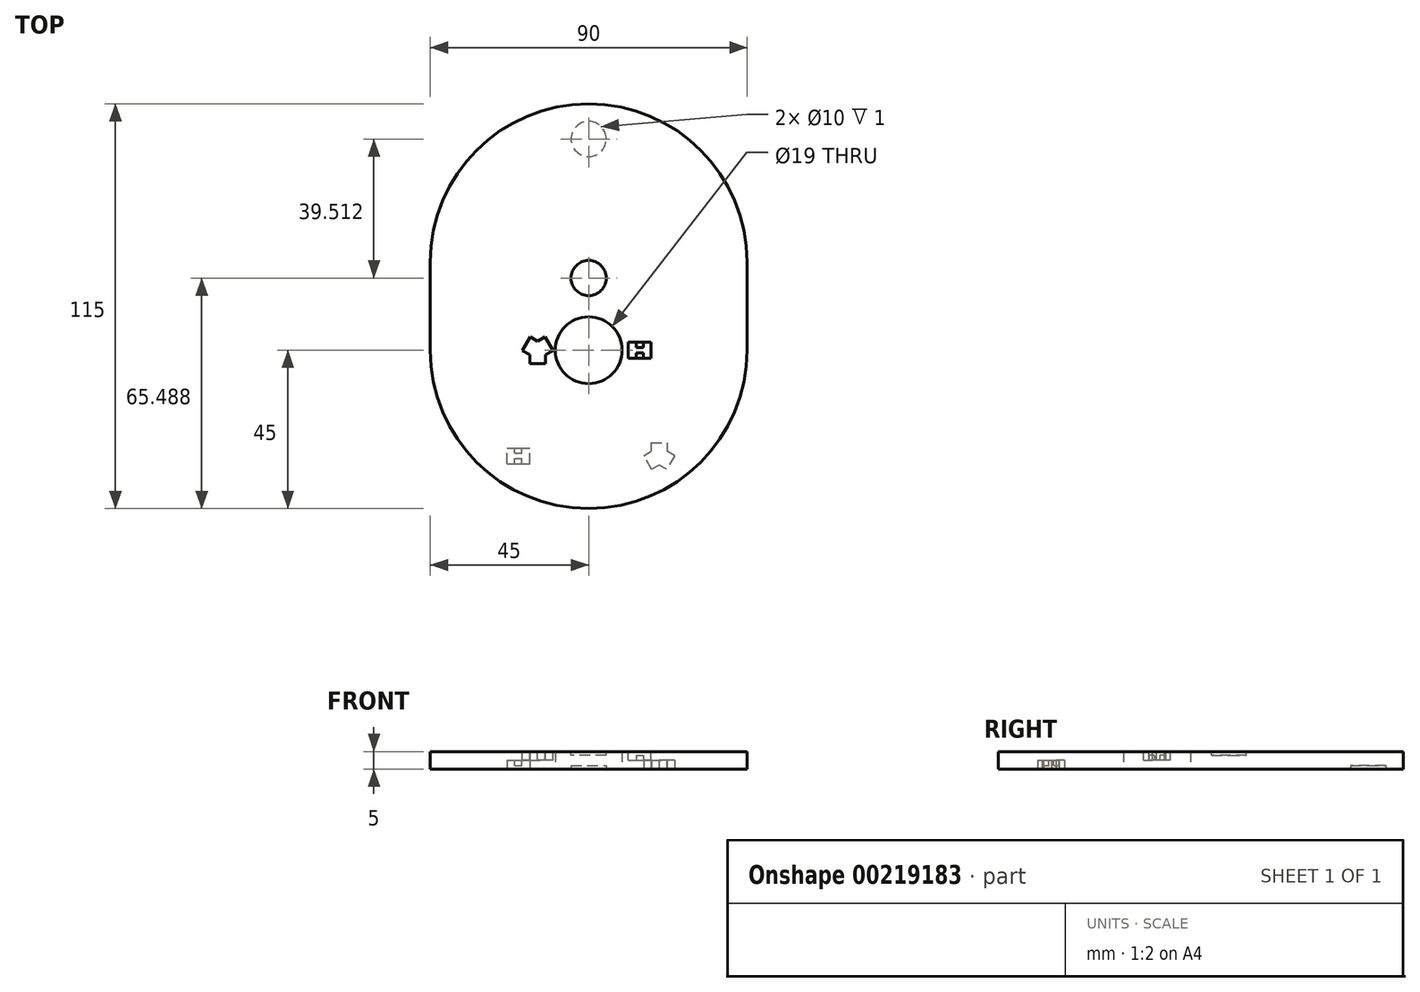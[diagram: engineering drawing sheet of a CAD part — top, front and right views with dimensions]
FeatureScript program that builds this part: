
annotation { "Feature Type Name" : "Feature", "Feature Type Description" : "" }
export const myFeature = defineFeature(function(context is Context, id is Id, definition is map)
    precondition{}
    {
        {
            var Q0;
            Q0=qCreatedBy(makeId("Top.planeOp"),FACE);
            var sketch = newSketch(context, id + "F0", { "sketchPlane" : qUnion([Q0])});
            skArc(sketch, "E0", {"start": v(-45, 0) * mm, "mid": v(0, -45) * mm, "end": v(45, 0) * mm});
            skLineSegment(sketch, "E1", {"start": v(-45, 0) * mm, "end": v(-45, 70) * mm});
            skLineSegment(sketch, "E2", {"start": v(-45, 70) * mm, "end": v(45, 70) * mm});
            skLineSegment(sketch, "E3", {"start": v(45, 70) * mm, "end": v(45, 0) * mm});
            skSolve(sketch);
        }
        {
            var Q0;
            Q0 = qSketchRegion(id + "F0", true);
            extrude(context, id + "F1", {"entities" : qUnion([Q0]), "depth" : 5 * mm});
        }
        {
            var Q0;
            Q0=makeQuery(id+"F1.opExtrude","CAP_FACE",FACE,{"disambiguationData":[OSD([sQuery(id+"F0.wireOp",EDGE,"E0")])],"isStart":false});
            var sketch = newSketch(context, id + "F2", { "sketchPlane" : qUnion([Q0])});
            skPoint(sketch, "E4", {"position": v(-14.5, 0) * mm});
            skLineSegment(sketch, "E5", {"start": v(-16.62, 3.83) * mm, "end": v(-18.87, -0.07) * mm});
            skLineSegment(sketch, "E6", {"start": v(-16.75, -3.75) * mm, "end": v(-12.25, -3.75) * mm});
            skLineSegment(sketch, "E7", {"start": v(-10.12, -0.07) * mm, "end": v(-12.37, 3.83) * mm});
            skLineSegment(sketch, "E8", {"start": v(-18.87, -0.07) * mm, "end": v(-16.75, -1.3) * mm});
            skLineSegment(sketch, "E9", {"start": v(-16.62, 3.83) * mm, "end": v(-14.5, 2.6) * mm});
            skLineSegment(sketch, "E10", {"start": v(-16.75, -3.75) * mm, "end": v(-16.75, -1.3) * mm});
            skLineSegment(sketch, "E11", {"start": v(-12.25, -3.75) * mm, "end": v(-12.25, -1.3) * mm});
            skLineSegment(sketch, "E12", {"start": v(-12.37, 3.83) * mm, "end": v(-14.5, 2.6) * mm});
            skLineSegment(sketch, "E13", {"start": v(-10.12, -0.07) * mm, "end": v(-12.25, -1.3) * mm});
            skPoint(sketch, "E14.orphan", {"position": v(-8, -3.75) * mm});
            skPoint(sketch, "E15.orphan", {"position": v(-14.5, 7.5) * mm});
            skPoint(sketch, "E16.orphan", {"position": v(-21, -3.75) * mm});
            skSolve(sketch);
        }
        {
            var Q0;
            Q0 = qSketchRegion(id + "F2", true);
            extrude(context, id + "F3", {"entities" : qUnion([Q0]), "operationType" : NewBodyOperationType.REMOVE, "oppositeDirection" : true, "depth" : 2.5 * mm});
        }
        {
            var Q0;
            Q0=makeQuery(id+"F1.opExtrude","CAP_FACE",FACE,{"disambiguationData":[OSD([sQuery(id+"F0.wireOp",EDGE,"E0")])],"isStart":false});
            var sketch = newSketch(context, id + "F4", { "sketchPlane" : qUnion([Q0])});
            skPoint(sketch, "E17", {"position": v(14.5, 0) * mm});
            skLineSegment(sketch, "E18.bottom", {"start": v(11.25, 2.25) * mm, "end": v(17.75, 2.25) * mm});
            skLineSegment(sketch, "E18.top", {"start": v(11.25, -2.25) * mm, "end": v(17.75, -2.25) * mm});
            skLineSegment(sketch, "E18.left", {"start": v(11.25, 2.25) * mm, "end": v(11.25, -2.25) * mm});
            skLineSegment(sketch, "E18.right", {"start": v(17.75, 2.25) * mm, "end": v(17.75, -2.25) * mm});
            skSolve(sketch);
        }
        {
            var Q0;
            Q0 = qSketchRegion(id + "F4", true);
            extrude(context, id + "F5", {"entities" : qUnion([Q0]), "operationType" : NewBodyOperationType.REMOVE, "oppositeDirection" : true, "depth" : 2.5 * mm});
        }
        {
            var Q0;
            Q0=makeQuery(id+"F5.boolean.opBoolean","COPY",FACE,{"derivedFrom":makeQuery(id+"F5.opExtrude","CAP_FACE",FACE,{"disambiguationData":[OSD([sQuery(id+"F4.wireOp",EDGE,"E18.bottom"),sQuery(id+"F4.wireOp",EDGE,"E18.top"),sQuery(id+"F4.wireOp",EDGE,"E18.left"),sQuery(id+"F4.wireOp",EDGE,"E18.right")])],"isStart":false})});
            var sketch = newSketch(context, id + "F6", { "sketchPlane" : qUnion([Q0])});
            skLineSegment(sketch, "E19.bottom", {"start": v(13.5, 2.25) * mm, "end": v(15.5, 2.25) * mm});
            skLineSegment(sketch, "E19.top", {"start": v(13.5, -2.25) * mm, "end": v(15.5, -2.25) * mm});
            skLineSegment(sketch, "E19.left", {"start": v(13.5, 2.25) * mm, "end": v(13.5, 0.75) * mm});
            skLineSegment(sketch, "E19.right", {"start": v(15.5, 2.25) * mm, "end": v(15.5, 0.75) * mm});
            skLineSegment(sketch, "E20", {"start": v(13.5, 0.75) * mm, "end": v(15.5, 0.75) * mm});
            skLineSegment(sketch, "E21", {"start": v(13.5, -0.75) * mm, "end": v(15.5, -0.75) * mm});
            skLineSegment(sketch, "E22.trimOffspring", {"start": v(13.5, -0.75) * mm, "end": v(13.5, -2.25) * mm});
            skLineSegment(sketch, "E23.trimOffspring", {"start": v(15.5, -0.75) * mm, "end": v(15.5, -2.25) * mm});
            skSolve(sketch);
        }
        {
            var Q0;
            Q0 = qSketchRegion(id + "F6", true);
            extrude(context, id + "F7", {"entities" : qUnion([Q0]), "operationType" : NewBodyOperationType.ADD, "depth" : 1.5 * mm});
        }
        {
            var Q0;
            Q0=makeQuery(id+"F1.opExtrude","CAP_FACE",FACE,{"disambiguationData":[OSD([sQuery(id+"F0.wireOp",EDGE,"E0")])],"isStart":false});
            var sketch = newSketch(context, id + "F8", { "sketchPlane" : qUnion([Q0])});
            skPoint(sketch, "E24", {"position": v(0, 20.49) * mm});
            skPoint(sketch, "E25", {"position": v(-14.5, 0) * mm});
            skCircle(sketch, "E26", {"center": v(0, 20.49) * mm, "radius": 5 * mm});
            skSolve(sketch);
        }
        {
            var Q0;
            Q0 = qSketchRegion(id + "F8", true);
            extrude(context, id + "F9", {"entities" : qUnion([Q0]), "operationType" : NewBodyOperationType.REMOVE, "oppositeDirection" : true, "depth" : 1 * mm});
        }
        {
            var Q0;
            Q0=makeQuery(id+"F1.opExtrude","CAP_FACE",FACE,{"disambiguationData":[OSD([sQuery(id+"F0.wireOp",EDGE,"E0")])],"isStart":true});
            var sketch = newSketch(context, id + "F10", { "sketchPlane" : qUnion([Q0])});
            skCircle(sketch, "E27", {"center": v(0, 0) * mm, "radius": 9.5 * mm});
            skSolve(sketch);
        }
        {
            var Q0;
            Q0 = qSketchRegion(id + "F10", true);
            extrude(context, id + "F11", {"entities" : qUnion([Q0]), "operationType" : NewBodyOperationType.REMOVE, "oppositeDirection" : true, "depth" : 10 * mm});
        }
        {
            var Q0;
            Q0=makeQuery(id+"F1.opExtrude","CAP_FACE",FACE,{"disambiguationData":[OSD([sQuery(id+"F0.wireOp",EDGE,"E0")])],"isStart":true});
            var sketch = newSketch(context, id + "F12", { "sketchPlane" : qUnion([Q0])});
            skCircle(sketch, "E28", {"center": v(0, -60) * mm, "radius": 5 * mm});
            skSolve(sketch);
        }
        {
            var Q0;
            Q0=makeQuery(id+"F1.opExtrude","CAP_FACE",FACE,{"disambiguationData":[OSD([sQuery(id+"F0.wireOp",EDGE,"E0"),sQuery(id+"F0.wireOp",EDGE,"E1"),sQuery(id+"F0.wireOp",EDGE,"E2"),sQuery(id+"F0.wireOp",EDGE,"E3")])],"isStart":true});
            var sketch = newSketch(context, id + "F13", { "sketchPlane" : qUnion([Q0])});
            skPoint(sketch, "E29", {"position": v(20, 30) * mm});
            skLineSegment(sketch, "E30", {"start": v(17.88, 33.83) * mm, "end": v(15.63, 29.93) * mm});
            skLineSegment(sketch, "E31", {"start": v(17.75, 26.25) * mm, "end": v(22.25, 26.25) * mm});
            skLineSegment(sketch, "E32", {"start": v(24.37, 29.93) * mm, "end": v(22.12, 33.83) * mm});
            skLineSegment(sketch, "E33", {"start": v(15.62, 29.93) * mm, "end": v(17.75, 28.7) * mm});
            skLineSegment(sketch, "E34", {"start": v(17.87, 33.83) * mm, "end": v(20, 32.6) * mm});
            skLineSegment(sketch, "E35", {"start": v(17.75, 26.25) * mm, "end": v(17.75, 28.7) * mm});
            skLineSegment(sketch, "E36", {"start": v(22.25, 26.25) * mm, "end": v(22.25, 28.7) * mm});
            skLineSegment(sketch, "E37", {"start": v(22.12, 33.83) * mm, "end": v(20, 32.6) * mm});
            skLineSegment(sketch, "E38", {"start": v(24.38, 29.93) * mm, "end": v(22.25, 28.7) * mm});
            skPoint(sketch, "E39.orphan", {"position": v(26.5, 26.25) * mm});
            skPoint(sketch, "E40.orphan", {"position": v(20, 37.5) * mm});
            skPoint(sketch, "E41.orphan", {"position": v(13.5, 26.25) * mm});
            skSolve(sketch);
        }
        {
            var Q0;
            Q0 = qSketchRegion(id + "F13", true);
            extrude(context, id + "F14", {"entities" : qUnion([Q0]), "operationType" : NewBodyOperationType.REMOVE, "oppositeDirection" : true, "depth" : 2.5 * mm});
        }
        {
            var Q0;
            Q0 = qSketchRegion(id + "F12", true);
            extrude(context, id + "F15", {"entities" : qUnion([Q0]), "operationType" : NewBodyOperationType.REMOVE, "oppositeDirection" : true, "depth" : 1 * mm});
        }
        {
            var Q0;
            Q0=makeQuery(id+"F1.opExtrude","CAP_FACE",FACE,{"disambiguationData":[OSD([sQuery(id+"F0.wireOp",EDGE,"E0"),sQuery(id+"F0.wireOp",EDGE,"E1"),sQuery(id+"F0.wireOp",EDGE,"E2"),sQuery(id+"F0.wireOp",EDGE,"E3")])],"isStart":true});
            var sketch = newSketch(context, id + "F16", { "sketchPlane" : qUnion([Q0])});
            skPoint(sketch, "E42", {"position": v(-20, 30) * mm});
            skLineSegment(sketch, "E43.bottom", {"start": v(-23.25, 32.25) * mm, "end": v(-16.75, 32.25) * mm});
            skLineSegment(sketch, "E43.top", {"start": v(-23.25, 27.75) * mm, "end": v(-16.75, 27.75) * mm});
            skLineSegment(sketch, "E43.left", {"start": v(-23.25, 32.25) * mm, "end": v(-23.25, 27.75) * mm});
            skLineSegment(sketch, "E43.right", {"start": v(-16.75, 32.25) * mm, "end": v(-16.75, 27.75) * mm});
            skSolve(sketch);
        }
        {
            var Q0;
            Q0 = qSketchRegion(id + "F16", true);
            extrude(context, id + "F17", {"entities" : qUnion([Q0]), "operationType" : NewBodyOperationType.REMOVE, "oppositeDirection" : true, "depth" : 2.5 * mm});
        }
        {
            var Q0;
            Q0=makeQuery(id+"F17.boolean.opBoolean","COPY",FACE,{"derivedFrom":makeQuery(id+"F17.opExtrude","CAP_FACE",FACE,{"disambiguationData":[OSD([sQuery(id+"F16.wireOp",EDGE,"E43.bottom"),sQuery(id+"F16.wireOp",EDGE,"E43.top"),sQuery(id+"F16.wireOp",EDGE,"E43.left"),sQuery(id+"F16.wireOp",EDGE,"E43.right")])],"isStart":false})});
            var sketch = newSketch(context, id + "F18", { "sketchPlane" : qUnion([Q0])});
            skLineSegment(sketch, "E44.bottom", {"start": v(-21, 32.25) * mm, "end": v(-19, 32.25) * mm});
            skLineSegment(sketch, "E44.top", {"start": v(-21, 27.75) * mm, "end": v(-19, 27.75) * mm});
            skLineSegment(sketch, "E44.left", {"start": v(-21, 32.25) * mm, "end": v(-21, 30.75) * mm});
            skLineSegment(sketch, "E44.right", {"start": v(-19, 32.25) * mm, "end": v(-19, 30.75) * mm});
            skLineSegment(sketch, "E45", {"start": v(-21, 30.75) * mm, "end": v(-19, 30.75) * mm});
            skLineSegment(sketch, "E46", {"start": v(-21, 29.25) * mm, "end": v(-19, 29.25) * mm});
            skLineSegment(sketch, "E47.trimOffspring", {"start": v(-21, 29.25) * mm, "end": v(-21, 27.75) * mm});
            skLineSegment(sketch, "E48.trimOffspring", {"start": v(-19, 29.25) * mm, "end": v(-19, 27.75) * mm});
            skSolve(sketch);
        }
        {
            var Q0;
            Q0 = qSketchRegion(id + "F18", true);
            extrude(context, id + "F19", {"entities" : qUnion([Q0]), "operationType" : NewBodyOperationType.ADD, "depth" : 1.5 * mm});
        }
        {
            var Q0;
            Q0=makeQuery(id+"F1.opExtrude","SWEPT_EDGE",EDGE,{"disambiguationData":[OSD([sQuery(id+"F0.wireOp",EDGE,"E1"),sQuery(id+"F0.wireOp",EDGE,"E2")])]});
            var Q1;
            Q1=makeQuery(id+"F1.opExtrude","SWEPT_EDGE",EDGE,{"disambiguationData":[OSD([sQuery(id+"F0.wireOp",EDGE,"E2"),sQuery(id+"F0.wireOp",EDGE,"E3")])]});
            fillet(context, id + "F20", {"entities" : qUnion([Q0, Q1]), "radius" : 45 * mm, "tangentPropagation" : true, "allowEdgeOverflow" : false});
        }
    });
